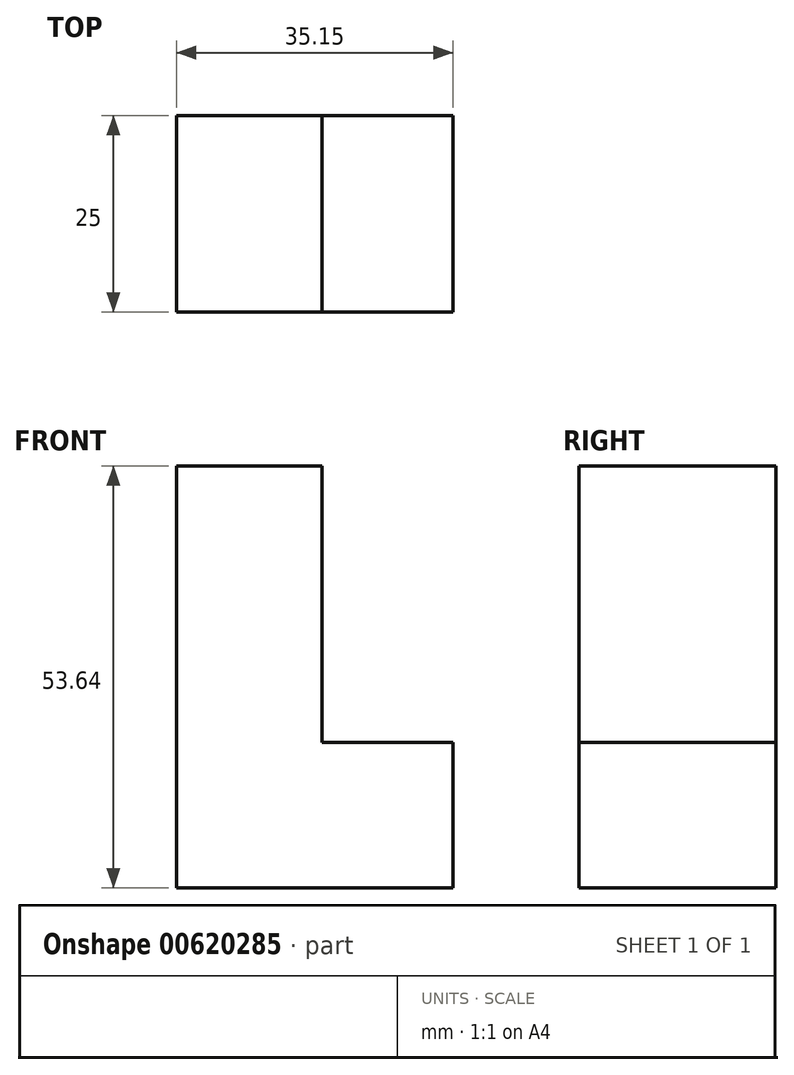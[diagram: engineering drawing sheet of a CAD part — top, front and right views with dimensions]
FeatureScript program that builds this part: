
annotation { "Feature Type Name" : "Feature", "Feature Type Description" : "" }
export const myFeature = defineFeature(function(context is Context, id is Id, definition is map)
    precondition{}
    {
        {
            var Q0;
            Q0=qCreatedBy(makeId("Front.planeOp"),FACE);
            var sketch = newSketch(context, id + "F0", { "sketchPlane" : qUnion([Q0])});
            skLineSegment(sketch, "E0", {"start": v(-55.94, 43.62) * mm, "end": v(-55.94, -10.02) * mm});
            skLineSegment(sketch, "E1", {"start": v(-55.94, -10.02) * mm, "end": v(-20.79, -10.02) * mm});
            skLineSegment(sketch, "E2", {"start": v(-20.79, -10.02) * mm, "end": v(-20.79, 8.45) * mm});
            skLineSegment(sketch, "E3", {"start": v(-20.79, 8.45) * mm, "end": v(-37.47, 8.45) * mm});
            skLineSegment(sketch, "E4", {"start": v(-37.47, 8.45) * mm, "end": v(-37.47, 43.62) * mm});
            skLineSegment(sketch, "E5", {"start": v(-37.47, 43.62) * mm, "end": v(-55.94, 43.62) * mm});
            skSolve(sketch);
        }
        {
            var Q0;
            Q0 = qSketchRegion(id + "F0", true);
            extrude(context, id + "F1", {"entities" : qUnion([Q0]), "depth" : 25 * mm, "offsetDistance" : 25 * mm});
        }
    });
